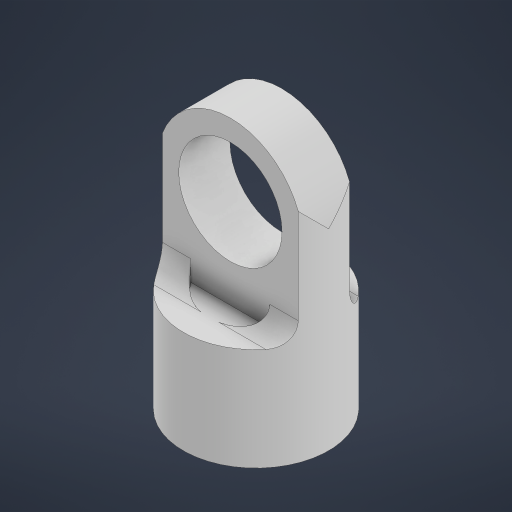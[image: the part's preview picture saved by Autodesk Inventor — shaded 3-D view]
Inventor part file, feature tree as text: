
AUTODESK INVENTOR PART (.ipt)
format: ipt  version: 2024 (Build 280153000, 153)  size: 232,960 bytes
history: native  units: in
note: dims shown in document units (in); Inventor stores cm internally (conversion verified against a paired STEP export)
features: projected_geometry x5, extrude x4, sketch x3, fillet x1
ambient origin geometry x8: Origin, YZ Plane, XZ Plane, XY Plane, X Axis, Y Axis, Z Axis, Center Point
bodies: Solid1 (feature_tree)
feature tree (13):
  extrude  "Extrusion1"  Depth=0.4331in
  extrude  "Extrusion2"  Depth=0.6693in
  sketch  "Sketch4"  dims[d5=0.4764in d6=0.2362in d7=0.0in d10=1.4734in d11=0.0in d12=0.0945in d13=0.0984in d14=0.0in]
  extrude  "Extrusion4"  Depth=0.0945in TaperAngle=0.0deg
  fillet  "Fillet1"  Radius=1.4734in
  extrude  "Extrusion5"  Depth=0.0945in
  sketch  "Sketch1"  dims[d0=0.6693in d1=0.4331in]
  sketch  "Sketch3"  dims[d2=0.4724in d3=0.0in d4=0.6693in]
  projected_geometry  "Projected Loop2"
  projected_geometry  "Projected Loop3"
  projected_geometry  "Projected Loop4"
  projected_geometry  "Projected Loop5"
  projected_geometry  "Projected Loop6"
